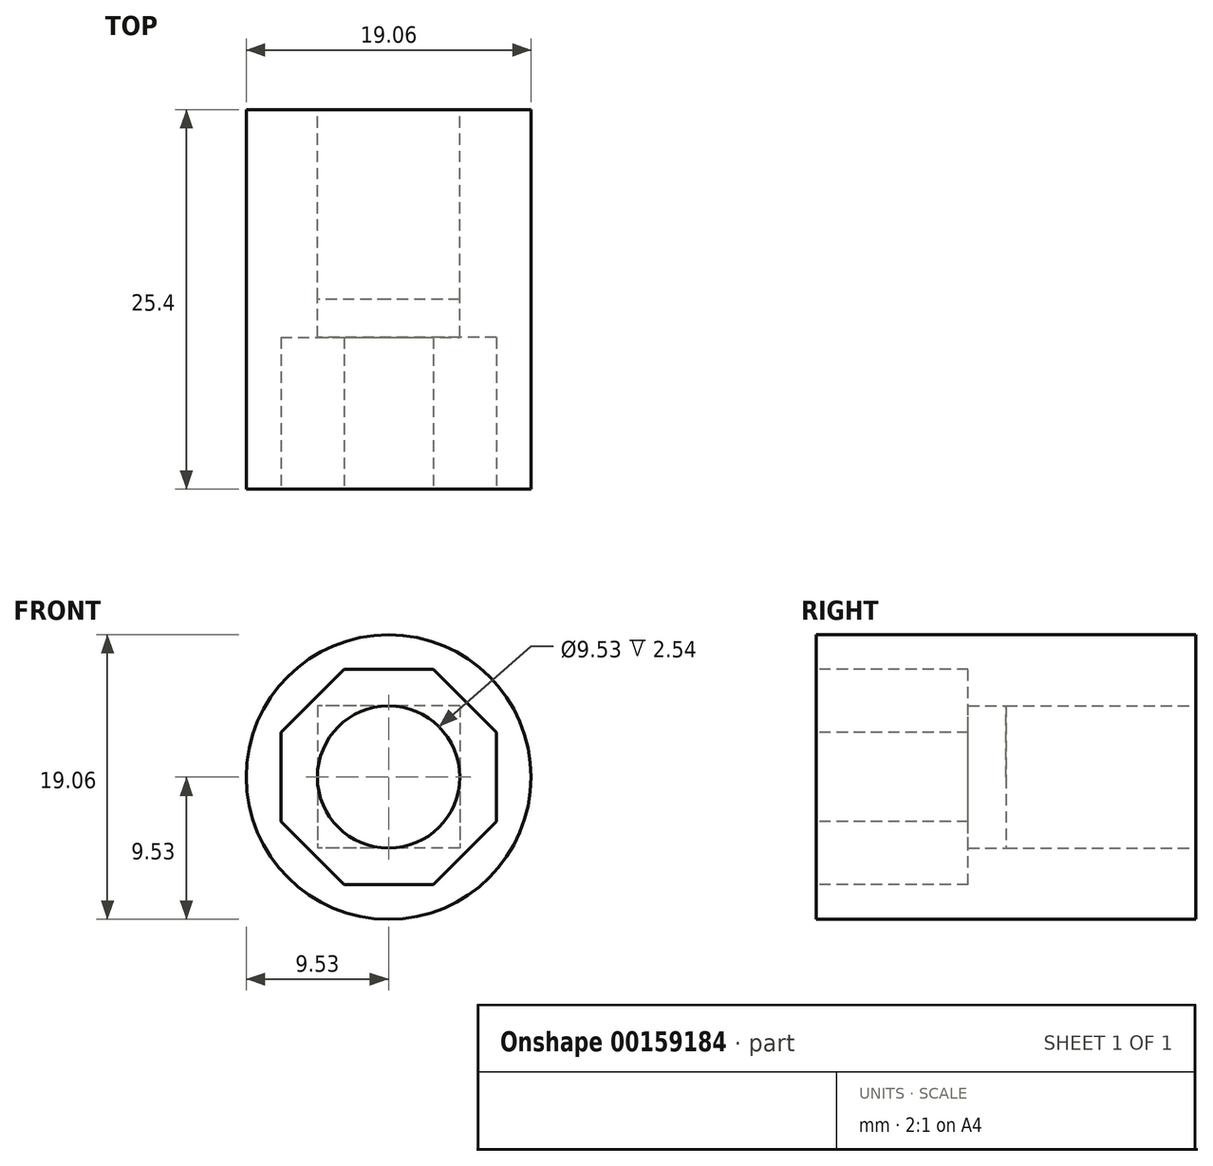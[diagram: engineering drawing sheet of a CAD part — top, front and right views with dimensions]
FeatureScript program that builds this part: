
annotation { "Feature Type Name" : "Feature", "Feature Type Description" : "" }
export const myFeature = defineFeature(function(context is Context, id is Id, definition is map)
    precondition{}
    {
        {
            var Q0;
            Q0=qCreatedBy(makeId("Front.planeOp"),FACE);
            var sketch = newSketch(context, id + "F0", { "sketchPlane" : qUnion([Q0])});
            skCircle(sketch, "E0", {"center": v(0, 0) * mm, "radius": 9.53 * mm});
            skSolve(sketch);
        }
        {
            var Q0;
            Q0=makeQuery(id+"F0.imprint","IMPRINT",FACE,{"disambiguationData":[TD([[makeQuery(id+"F0.imprint","IMPRINT",EDGE,{"derivedFrom":sQuery(id+"F0.wireOp",EDGE,"E0")}),1.0]])]});
            extrude(context, id + "F1", {"entities" : qUnion([Q0]), "depth" : 25.4 * mm});
        }
        {
            var Q0;
            Q0=qCreatedBy(makeId("Front.planeOp"),FACE);
            var sketch = newSketch(context, id + "F2", { "sketchPlane" : qUnion([Q0])});
            skLineSegment(sketch, "E1.bottom", {"start": v(4.76, 4.76) * mm, "end": v(-4.76, 4.76) * mm});
            skLineSegment(sketch, "E1.top", {"start": v(4.76, -4.76) * mm, "end": v(-4.76, -4.76) * mm});
            skLineSegment(sketch, "E1.left", {"start": v(4.76, 4.76) * mm, "end": v(4.76, -4.76) * mm});
            skLineSegment(sketch, "E1.right", {"start": v(-4.76, 4.76) * mm, "end": v(-4.76, -4.76) * mm});
            skPoint(sketch, "E1.middle", {"position": v(0, 0) * mm});
            skCircle(sketch, "E2", {"center": v(0, 0) * mm, "radius": 4.76 * mm});
            skSolve(sketch);
        }
        {
            var Q0;
            {var subQ0=sQuery(id+"F2.wireOp",EDGE,"E2");var subQ1=makeQuery(id+"F2.imprint","INTERSECT",VERTEX,{"derivedFrom":[sQuery(id+"F2.wireOp",EDGE,"E1.bottom"),subQ0]});Q0=makeQuery(id+"F2.imprint","IMPRINT",FACE,{"disambiguationData":[TD([[makeQuery(id+"F2.imprint","IMPRINT",EDGE,{"disambiguationData":[TD([[subQ1,1.0]])],"derivedFrom":subQ0}),1.0]])]});}
            extrude(context, id + "F3", {"entities" : qUnion([Q0]), "operationType" : NewBodyOperationType.REMOVE, "endBound" : BoundingType.THROUGH_ALL, "depth" : 25.4 * mm});
        }
        {
            var Q0;
            Q0 = qSketchRegion(id + "F2", true);
            extrude(context, id + "F4", {"entities" : qUnion([Q0]), "operationType" : NewBodyOperationType.REMOVE, "depth" : 12.7 * mm});
        }
        {
            var Q0;
            Q0=makeQuery(id+"F1.opExtrude","CAP_FACE",FACE,{"disambiguationData":[OSD([sQuery(id+"F0.wireOp",EDGE,"E0")])],"isStart":false});
            var sketch = newSketch(context, id + "F5", { "sketchPlane" : qUnion([Q0])});
            skCircle(sketch, "E3.cCircle", {"center": v(0, 0) * mm, "radius": 7.21 * mm, "construction": true});
            skLineSegment(sketch, "E3.0", {"start": v(-2.99, 7.21) * mm, "end": v(2.99, 7.21) * mm});
            skLineSegment(sketch, "E3.1", {"start": v(2.99, 7.21) * mm, "end": v(7.21, 2.99) * mm});
            skLineSegment(sketch, "E3.2", {"start": v(7.21, 2.99) * mm, "end": v(7.21, -2.99) * mm});
            skLineSegment(sketch, "E3.3", {"start": v(7.21, -2.99) * mm, "end": v(2.99, -7.21) * mm});
            skLineSegment(sketch, "E3.4", {"start": v(2.99, -7.21) * mm, "end": v(-2.99, -7.21) * mm});
            skLineSegment(sketch, "E3.5", {"start": v(-2.99, -7.21) * mm, "end": v(-7.21, -2.99) * mm});
            skLineSegment(sketch, "E3.6", {"start": v(-7.21, -2.99) * mm, "end": v(-7.21, 2.99) * mm});
            skLineSegment(sketch, "E3.7", {"start": v(-7.21, 2.99) * mm, "end": v(-2.99, 7.21) * mm});
            skPoint(sketch, "E3.0.midPoint", {"position": v(0, 7.21) * mm});
            skSolve(sketch);
        }
        {
            var Q0;
            Q0=makeQuery(id+"F5.imprint","IMPRINT",FACE,{"disambiguationData":[TD([[makeQuery(id+"F5.imprint","IMPRINT",EDGE,{"derivedFrom":sQuery(id+"F5.wireOp",EDGE,"E3.0")}),-1.0]])]});
            extrude(context, id + "F6", {"entities" : qUnion([Q0]), "operationType" : NewBodyOperationType.REMOVE, "oppositeDirection" : true, "depth" : 10.16 * mm});
        }
    });
